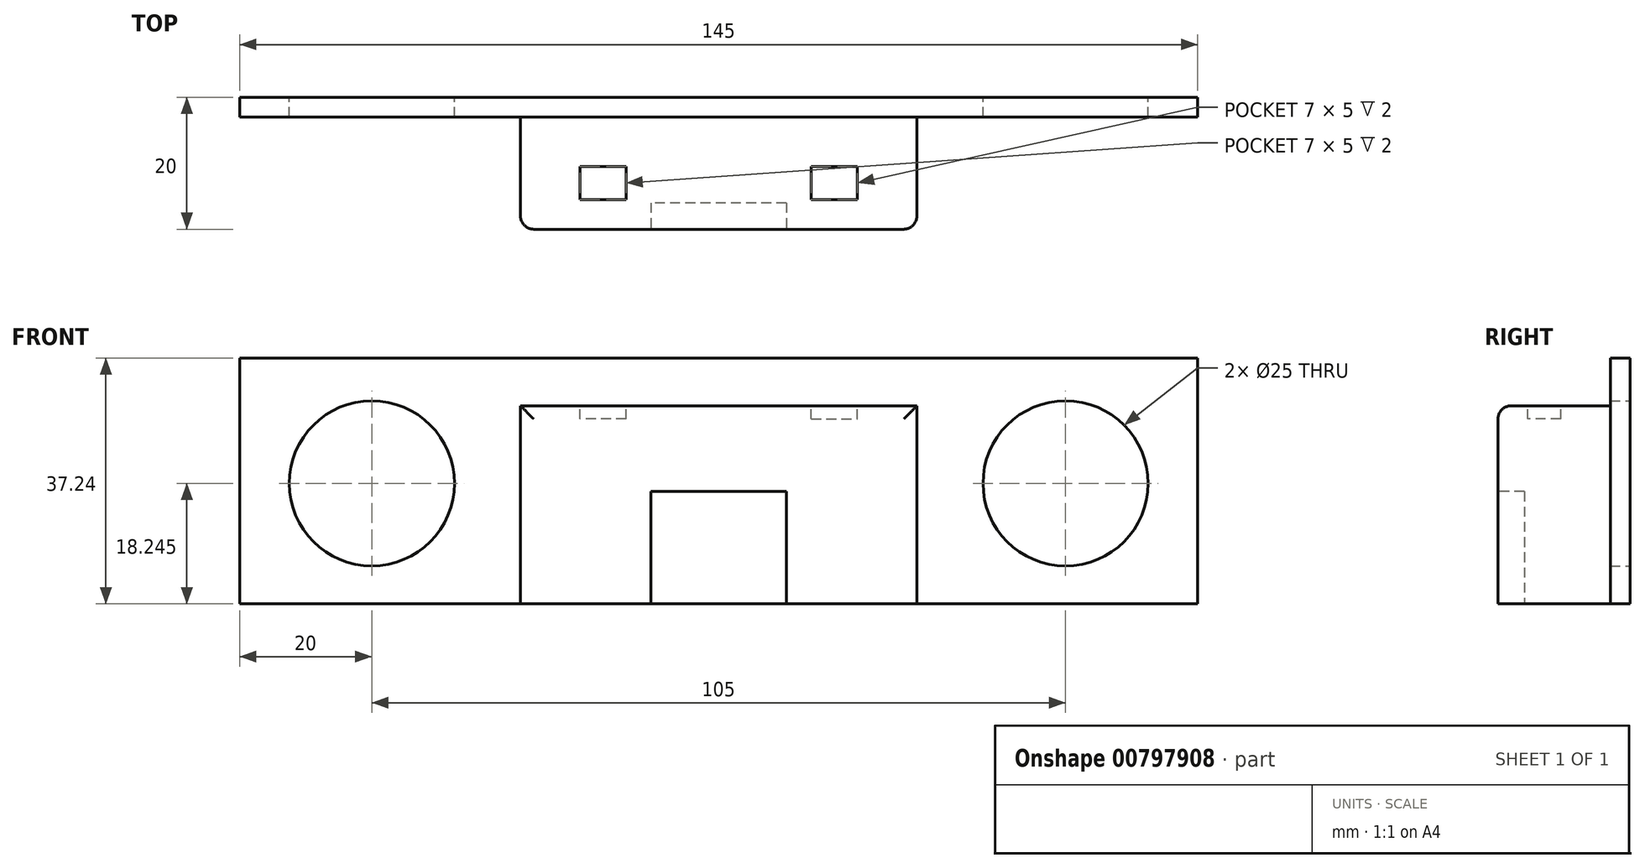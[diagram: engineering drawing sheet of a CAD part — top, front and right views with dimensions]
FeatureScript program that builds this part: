
annotation { "Feature Type Name" : "Feature", "Feature Type Description" : "" }
export const myFeature = defineFeature(function(context is Context, id is Id, definition is map)
    precondition{}
    {
        {
            var Q0;
            Q0=qCreatedBy(makeId("Front.planeOp"),FACE);
            var sketch = newSketch(context, id + "F0", { "sketchPlane" : qUnion([Q0])});
            skLineSegment(sketch, "E0.bottom", {"start": v(72.5, 18.62) * mm, "end": v(-72.5, 18.62) * mm});
            skLineSegment(sketch, "E0.top", {"start": v(72.5, -18.62) * mm, "end": v(-72.5, -18.62) * mm});
            skLineSegment(sketch, "E0.left", {"start": v(72.5, 18.62) * mm, "end": v(72.5, -18.62) * mm});
            skLineSegment(sketch, "E0.right", {"start": v(-72.5, 18.62) * mm, "end": v(-72.5, -18.62) * mm});
            skPoint(sketch, "E0.middle", {"position": v(0, 0) * mm});
            skCircle(sketch, "E1", {"center": v(52.5, -0.37) * mm, "radius": 12.5 * mm});
            skCircle(sketch, "E2", {"center": v(-52.5, -0.37) * mm, "radius": 12.5 * mm});
            skSolve(sketch);
        }
        {
            var Q0;
            Q0=qSketchRegion(id+"F0",true);
            extrude(context, id + "F1", {"entities" : qUnion([Q0]), "depth" : 3 * mm});
        }
        {
            var Q0;
            Q0=makeQuery(id+"F1.opExtrude","CAP_FACE",FACE,{"disambiguationData":[OSD([sQuery(id+"F0.wireOp",EDGE,"E0.bottom"),sQuery(id+"F0.wireOp",EDGE,"E0.top"),sQuery(id+"F0.wireOp",EDGE,"E0.left"),sQuery(id+"F0.wireOp",EDGE,"E0.right"),sQuery(id+"F0.wireOp",EDGE,"sOKRK9WS-TzGH-iPKk-9lGy-1haYnsqfv4Nf"),sQuery(id+"F0.wireOp",EDGE,"94ZFEkxM-q5Sw-y5fY-uU9Y-FHWCruAk6SLc")])],"isStart":false});
            var sketch = newSketch(context, id + "F2", { "sketchPlane" : qUnion([Q0])});
            skLineSegment(sketch, "E3.bottom", {"start": v(-30, 11.37) * mm, "end": v(30, 11.38) * mm});
            skLineSegment(sketch, "E3.top", {"start": v(-30, -18.63) * mm, "end": v(30, -18.62) * mm});
            skLineSegment(sketch, "E3.left", {"start": v(-30, 11.37) * mm, "end": v(-30, -18.63) * mm});
            skLineSegment(sketch, "E3.right", {"start": v(30, 11.38) * mm, "end": v(30, -18.62) * mm});
            skSolve(sketch);
        }
        {
            var Q0;
            Q0=qSketchRegion(id+"F2",true);
            extrude(context, id + "F3", {"entities" : qUnion([Q0]), "operationType" : NewBodyOperationType.ADD, "depth" : 17 * mm});
        }
        {
            var Q0;
            Q0=makeQuery(id+"F3.opExtrude","SWEPT_FACE",FACE,{"disambiguationData":[OSD([sQuery(id+"F2.wireOp",EDGE,"E3.bottom")])]});
            var sketch = newSketch(context, id + "F4", { "sketchPlane" : qUnion([Q0])});
            skLineSegment(sketch, "E4.bottom", {"start": v(17.5, -13) * mm, "end": v(-17.5, -13) * mm, "construction": true});
            skLineSegment(sketch, "E4.top", {"start": v(17.5, -13) * mm, "end": v(-17.5, -13) * mm, "construction": true});
            skLineSegment(sketch, "E4.left", {"start": v(17.5, -13) * mm, "end": v(17.5, -13) * mm});
            skLineSegment(sketch, "E4.right", {"start": v(-17.5, -13) * mm, "end": v(-17.5, -13) * mm});
            skPoint(sketch, "E4.middle", {"position": v(0, -13) * mm});
            skLineSegment(sketch, "E5.bottom", {"start": v(-14, -10.5) * mm, "end": v(-21, -10.5) * mm});
            skLineSegment(sketch, "E5.top", {"start": v(-14, -15.5) * mm, "end": v(-21, -15.5) * mm});
            skLineSegment(sketch, "E5.left", {"start": v(-14, -10.5) * mm, "end": v(-14, -15.5) * mm});
            skLineSegment(sketch, "E5.right", {"start": v(-21, -10.5) * mm, "end": v(-21, -15.5) * mm});
            skPoint(sketch, "E5.middle", {"position": v(-17.5, -13) * mm});
            skLineSegment(sketch, "E6.bottom", {"start": v(14, -10.5) * mm, "end": v(21, -10.5) * mm});
            skLineSegment(sketch, "E6.top", {"start": v(14, -15.5) * mm, "end": v(21, -15.5) * mm});
            skLineSegment(sketch, "E6.left", {"start": v(14, -10.5) * mm, "end": v(14, -15.5) * mm});
            skLineSegment(sketch, "E6.right", {"start": v(21, -10.5) * mm, "end": v(21, -15.5) * mm});
            skPoint(sketch, "E6.middle", {"position": v(17.5, -13) * mm});
            skSolve(sketch);
        }
        {
            var Q0;
            Q0=qSketchRegion(id+"F4",true);
            extrude(context, id + "F5", {"entities" : qUnion([Q0]), "operationType" : NewBodyOperationType.REMOVE, "oppositeDirection" : true, "depth" : 2 * mm});
        }
        {
            var Q0;
            Q0=makeQuery(id+"F3.opExtrude","CAP_EDGE",EDGE,{"disambiguationData":[OSD([sQuery(id+"F2.wireOp",EDGE,"E3.bottom")])],"isStart":true});
            var Q1;
            Q1=makeQuery(id+"F3.opExtrude","CAP_EDGE",EDGE,{"disambiguationData":[OSD([sQuery(id+"F2.wireOp",EDGE,"E3.right")])],"isStart":true});
            var Q2;
            Q2=makeQuery(id+"F3.opExtrude","CAP_EDGE",EDGE,{"disambiguationData":[OSD([sQuery(id+"F2.wireOp",EDGE,"E3.left")])],"isStart":true});
            var Q3;
            Q3=makeQuery(id+"F3.opExtrude","CAP_EDGE",EDGE,{"disambiguationData":[OSD([sQuery(id+"F2.wireOp",EDGE,"E3.left")])],"isStart":false});
            var Q4;
            Q4=makeQuery(id+"F3.opExtrude","CAP_EDGE",EDGE,{"disambiguationData":[OSD([sQuery(id+"F2.wireOp",EDGE,"E3.bottom")])],"isStart":false});
            var Q5;
            Q5=makeQuery(id+"F3.opExtrude","CAP_EDGE",EDGE,{"disambiguationData":[OSD([sQuery(id+"F2.wireOp",EDGE,"E3.right")])],"isStart":false});
            fillet(context, id + "F6", {"entities" : qUnion([Q0, Q1, Q2, Q3, Q4, Q5]), "radius" : 2 * mm, "tangentPropagation" : true, "allowEdgeOverflow" : false});
        }
        {
            var Q0;
            Q0=makeQuery(id+"F3.opExtrude","CAP_FACE",FACE,{"disambiguationData":[OSD([sQuery(id+"F2.wireOp",EDGE,"E3.bottom"),sQuery(id+"F2.wireOp",EDGE,"E3.top"),sQuery(id+"F2.wireOp",EDGE,"E3.left"),sQuery(id+"F2.wireOp",EDGE,"E3.right")])],"isStart":false});
            var sketch = newSketch(context, id + "F7", { "sketchPlane" : qUnion([Q0])});
            skLineSegment(sketch, "E7.bottom", {"start": v(10.25, -1.62) * mm, "end": v(-10.25, -1.62) * mm});
            skLineSegment(sketch, "E7.top", {"start": v(10.25, -18.62) * mm, "end": v(-10.25, -18.62) * mm});
            skLineSegment(sketch, "E7.left", {"start": v(10.25, -1.62) * mm, "end": v(10.25, -18.62) * mm});
            skLineSegment(sketch, "E7.right", {"start": v(-10.25, -1.62) * mm, "end": v(-10.25, -18.62) * mm});
            skPoint(sketch, "E7.middle", {"position": v(0, -10.12) * mm});
            skSolve(sketch);
        }
        {
            var Q0;
            Q0 = qSketchRegion(id + "F7", true);
            extrude(context, id + "F8", {"entities" : qUnion([Q0]), "operationType" : NewBodyOperationType.REMOVE, "oppositeDirection" : true, "depth" : 4 * mm, "offsetDistance" : 25 * mm});
        }
    });
